# Revit family: PLASTIC SAND TRAP BASE DN100 Grate
name_source: partatom
category: Оборудование
units: mm (PartAtom-declared; Revit-internal decimal feet)

## family parameters
Общий = Да
Основа = Грань
При загрузке вырезать с полостями = Нет
Размер круглого соединителя = Использовать диаметр
Тип детали = Нормальный
Точка расчета площади = Нет

## types (2) — shared parameters
A10-01 = Stainless Steel Mesh ADA B125 : 20552
A10-02 = Stainless Steel Heelproof A15 : 205518
A10-03 = Stainless Steel Heelproof A15 screw fastening : 2055181
A10-04 = Stainless Steel Mesh A15 : 205516
A10-05 = Stainless Steel Mesh ADA A15 : 2055
A10-06 = Stainless steel slotted A15 : 2095
A10-07 = Stainless steel slotted for fastener A15 : 20951
A10-08 = Brass slotted A15 : 2075
A10-09 = Brass slotted for fastener A15 : 20751
A10-10 = Copper slotted A15 : 2065
A10-11 = Copper slotted for fastener A15 : 20651
A10-12 = Galvanized Steel Mesh ADA B125 : 20252
A10-13 = Galvanized Steel Heelproof A15 : 202518
A10-14 = Galvanized Steel Heelproof A15 screw fastening : 2025181
A10-15 = Galvanized Steel Mesh A15 : 202516
A10-16 = Galvanized Steel Mesh ADA A15 : 2025
A10-17 = Galvanized steel slotted A15 : 2015
A10-18 = Galvanized steel slotted for fastener A15 : 20151
A5-01 = Cast iron mesh В125 : 20402
A5-02 = Cast iron slotted ADA С250 : 20403-ADA
A5-03 = Cast iron slotted С250 : 283031
A5-04 = Cast iron slotted anti-slip С250 : 20303
A5-05 = Cast iron slotted Protector С250 : 203032
A5-06 = Cast iron slotted Wave С250 : 2030351
A5-07 = Plastic slotted A15 : 208019
ADSK_Dimension_Diameter = 100 мм
ADSK_Dimension_Width = 156 мм
ADSK_Load class = C250
ADSK_Manufacturer = Vodaland
ADSK_Material_Name = Plastic
ADSK_Sealant = 11
ADSK_Unit = pcs
ADSK_Weight = 2.6
Channel = Plastic sand trap Base DN100 : 8080
ConnectorBack = TC : Back
ConnectorFront = TC : Front
ConnectorLeft = TC : Left
ConnectorRight = TC : Right
Dp110 = Dp : 110
Dp160 = Dp : 160
Dp50 = Dp : 50
Fa1 = Choice of fastening : 6100-35
Fa2 = Choice of fastening : 6200-35
Fr1 = Fastening : 6100-35
Fr2 = Fastening : 6200-35
Fr3 = Fastening : 6800-35
G10-01 = Stainless Steel Grate Base DN100 Mesh ADA B125 0,5 m : 20552
G10-02 = Stainless Steel Grate Base DN100 Heelproof A15 0,5 m : 205518
G10-03 = Stainless Steel Grate Base DN100 Heelproof A15 screw fastening 0,5 m : 2055181
G10-04 = Stainless Steel Grate Base DN100 Mesh A15 0,5 m : 205516
G10-05 = Stainless Steel Grate Base DN100 Mesh ADA A15 0,5 m : 2055
G10-06 = Stainless steel grate Base DN100 slotted A15 0,5 m : 2095
G10-07 = Stainless steel grate Base DN100 slotted for fastener A15 0,5 m : 20951
G10-08 = Brass grate Base DN100 slotted A15 0,5 m : 2075
G10-09 = Brass grate Base DN100 slotted for fastener A15 0,5 m : 20751
G10-10 = Copper grate Base DN100 slotted A15 0,5 m : 2065
G10-11 = Copper grate Base DN100 slotted for fastener A15 0,5 m : 20651
G10-12 = Galvanized Steel Grate Base DN100 Mesh ADA B125 0,5 m : 20252
G10-13 = Galvanized Steel Grate Base DN100 Heelproof A15 0,5 m : 202518
G10-14 = Galvanized Steel Grate Base DN100 Heelproof A15 screw fastening 0,5 m : 2025181
G10-15 = Galvanized Steel Grate Base DN100 Mesh A15 0,5 m : 202516
G10-16 = Galvanized Steel Grate Base DN100 Mesh ADA A15 0,5 m : 2025
G10-17 = Galvanized steel grate Base DN100 slotted A15 0,5 m : 2015
G10-18 = Galvanized steel grate Base DN100 slotted for fastener A15 0,5 m : 20151
G5-01 = Cast iron grate Base DN100 mesh В125 : 20402
G5-02 = Cast iron grate Base DN100 slotted ADA С250 : 20403-ADA
G5-03 = Cast iron grate Base DN100 slotted С250 : 283031
G5-04 = Cast iron grate Base DN100 slotted anti-slip С250 : 20303
G5-05 = Cast iron grate Base DN100 slotted Protector С250 : 203032
G5-06 = Cast iron grate Base DN100 slotted Wave С250 : 2030351
G5-07 = Plastic grate Base DN100 slotted A15 : 208019
W1 = 160 мм
W2 = 156 мм
no = No
Группа модели = Linear drainage
zero-valued in all types: Отметка по умолчанию

## per-type parameters (varying)
| type | ADSK_Dimension_Height | ADSK_Dimension_Lenght | ADSK_Name |
| 8080 | 350 мм | 500 мм | Plastic sand trap Base DN100 H350 |
| 8087 | 400 мм | 507 мм | Plastic sand trap Base DN100 H500 reinforced |

note: column(s) folded — value = type name in every type: ADSK_Product code

## geometry (parser evidence)
native form markers: Blend x6
no freeform markers — native parametric forms only
